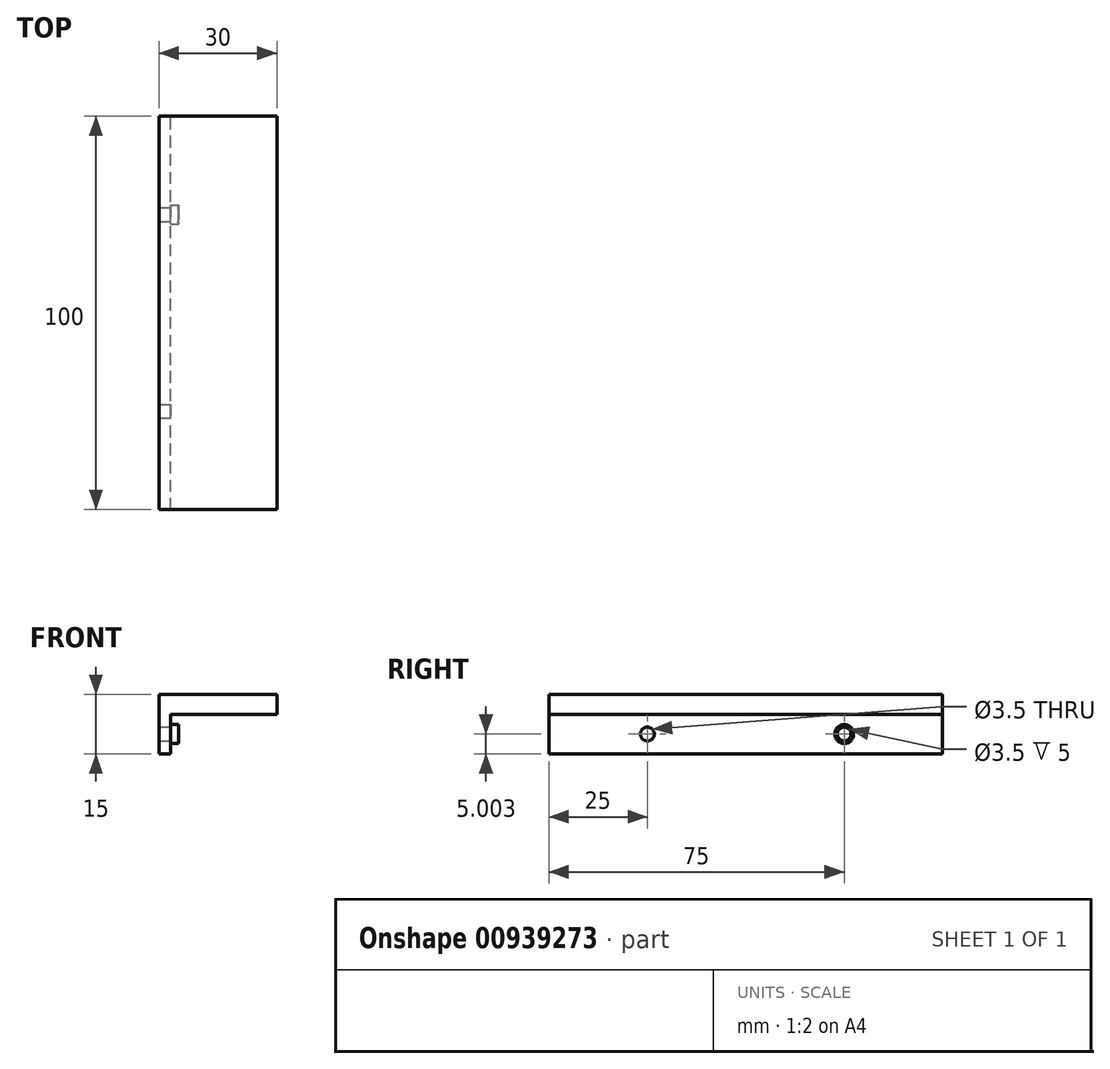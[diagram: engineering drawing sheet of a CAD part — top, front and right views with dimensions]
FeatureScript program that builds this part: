
annotation { "Feature Type Name" : "Feature", "Feature Type Description" : "" }
export const myFeature = defineFeature(function(context is Context, id is Id, definition is map)
    precondition{}
    {
        {
            var Q0;
            Q0=qCreatedBy(makeId("Front.planeOp"),FACE);
            var sketch = newSketch(context, id + "F0", { "sketchPlane" : qUnion([Q0])});
            skLineSegment(sketch, "E0", {"start": v(-9.97, -6.89) * mm, "end": v(-4.97, -6.89) * mm});
            skLineSegment(sketch, "E1", {"start": v(-4.97, -6.89) * mm, "end": v(-4.97, 3.11) * mm});
            skLineSegment(sketch, "E2", {"start": v(-4.97, 3.11) * mm, "end": v(20.03, 3.11) * mm});
            skLineSegment(sketch, "E3", {"start": v(20.03, 3.11) * mm, "end": v(20.03, 8.11) * mm});
            skLineSegment(sketch, "E4", {"start": v(20.03, 8.11) * mm, "end": v(-9.97, 8.11) * mm});
            skLineSegment(sketch, "E5", {"start": v(-9.97, 8.11) * mm, "end": v(-9.97, -6.89) * mm});
            skSolve(sketch);
        }
        {
            var Q0;
            Q0=makeQuery(id+"F0.imprint","IMPRINT",FACE,{"disambiguationData":[TD([[makeQuery(id+"F0.imprint","IMPRINT",EDGE,{"derivedFrom":sQuery(id+"F0.wireOp",EDGE,"E0")}),1.0]])]});
            extrude(context, id + "F1", {"entities" : qUnion([Q0]), "endBound" : BoundingType.SYMMETRIC, "depth" : 100 * mm, "offsetDistance" : 25 * mm});
        }
        {
            var Q0;
            Q0=makeQuery(id+"F1.opExtrude","SWEPT_FACE",FACE,{"disambiguationData":[OSD([sQuery(id+"F0.wireOp",EDGE,"E1")])]});
            var sketch = newSketch(context, id + "F2", { "sketchPlane" : qUnion([Q0])});
            skPoint(sketch, "E6", {"position": v(-25, -1.89) * mm});
            skPoint(sketch, "E7.MirrorP", {"position": v(25, -1.89) * mm});
            skSolve(sketch);
        }
        {
            var Q0;
            Q0=sQuery(id+"F2.wireOp",VERTEX,"E6");
            var Q1;
            Q1=sQuery(id+"F2.wireOp",VERTEX,"E7.MirrorP");
            var Q2;
            Q2=makeQuery(id+"F1.opExtrude","SWEPT_BODY",BODY,{"disambiguationData":[OSD([sQuery(id+"F0.wireOp",EDGE,"E0"),sQuery(id+"F0.wireOp",EDGE,"E1"),sQuery(id+"F0.wireOp",EDGE,"E2"),sQuery(id+"F0.wireOp",EDGE,"E3"),sQuery(id+"F0.wireOp",EDGE,"E4"),sQuery(id+"F0.wireOp",EDGE,"E5")])]});
            hole(context, id + "F3", {"style" : HoleStyle.SIMPLE, "endStyle" : HoleEndStyle.THROUGH, "holeDiameter" : 3.5 * mm, "majorDiameter" : 5 * mm, "isTappedThrough" : true, "tappedDepth" : 12 * mm, "tapClearance" : 3, "locations" : qUnion([Q0, Q1]), "scope" : qUnion([Q2])});
        }
        {
            var Q0;
            Q0=makeQuery(id+"F1.opExtrude","SWEPT_FACE",FACE,{"disambiguationData":[OSD([sQuery(id+"F0.wireOp",EDGE,"E1")])]});
            var sketch = newSketch(context, id + "F4", { "sketchPlane" : qUnion([Q0])});
            skCircle(sketch, "E8", {"center": v(-25, -1.89) * mm, "radius": 2.4 * mm});
            skCircle(sketch, "E9.MirrorC", {"center": v(25, -1.89) * mm, "radius": 2.4 * mm});
            skSolve(sketch);
        }
        {
            var Q0;
            Q0=makeQuery(id+"F4.imprint","IMPRINT",FACE,{"disambiguationData":[TD([[makeQuery(id+"F4.imprint","IMPRINT",EDGE,{"derivedFrom":makeQuery(id+"F3.hole-0.boolean.opBoolean","COPY",EDGE,{"derivedFrom":makeQuery(id+"F3.hole-0.opRevolve","SWEPT_EDGE",EDGE,{"disambiguationData":[OSD([sQuery(id+"F3.hole-0.sketch.wireOp",EDGE,"core_line_2"),sQuery(id+"F3.hole-0.sketch.wireOp",EDGE,"core_line_3")])]})})}),1.0]])]});
            var Q1;
            Q1=makeQuery(id+"F4.imprint","IMPRINT",FACE,{"disambiguationData":[TD([[makeQuery(id+"F4.imprint","IMPRINT",EDGE,{"derivedFrom":makeQuery(id+"F3.hole-1.boolean.opBoolean","COPY",EDGE,{"derivedFrom":makeQuery(id+"F3.hole-1.opRevolve","SWEPT_EDGE",EDGE,{"disambiguationData":[OSD([sQuery(id+"F3.hole-1.sketch.wireOp",EDGE,"core_line_2"),sQuery(id+"F3.hole-1.sketch.wireOp",EDGE,"core_line_3")])]})})}),1.0]])]});
            var Q2;
            Q2=makeQuery(id+"F4.imprint","IMPRINT",FACE,{"disambiguationData":[TD([[makeQuery(id+"F4.imprint","IMPRINT",EDGE,{"derivedFrom":sQuery(id+"F4.wireOp",EDGE,"E8")}),1.0]])]});
            var Q3;
            Q3=makeQuery(id+"F4.imprint","IMPRINT",FACE,{"disambiguationData":[TD([[makeQuery(id+"F4.imprint","IMPRINT",EDGE,{"derivedFrom":sQuery(id+"F4.wireOp",EDGE,"E9.MirrorC")}),-1.0]])]});
            extrude(context, id + "F5", {"entities" : qUnion([Q0, Q1, Q2, Q3]), "operationType" : NewBodyOperationType.REMOVE, "oppositeDirection" : true, "depth" : 2 * mm, "offsetDistance" : 25 * mm});
        }
    });
